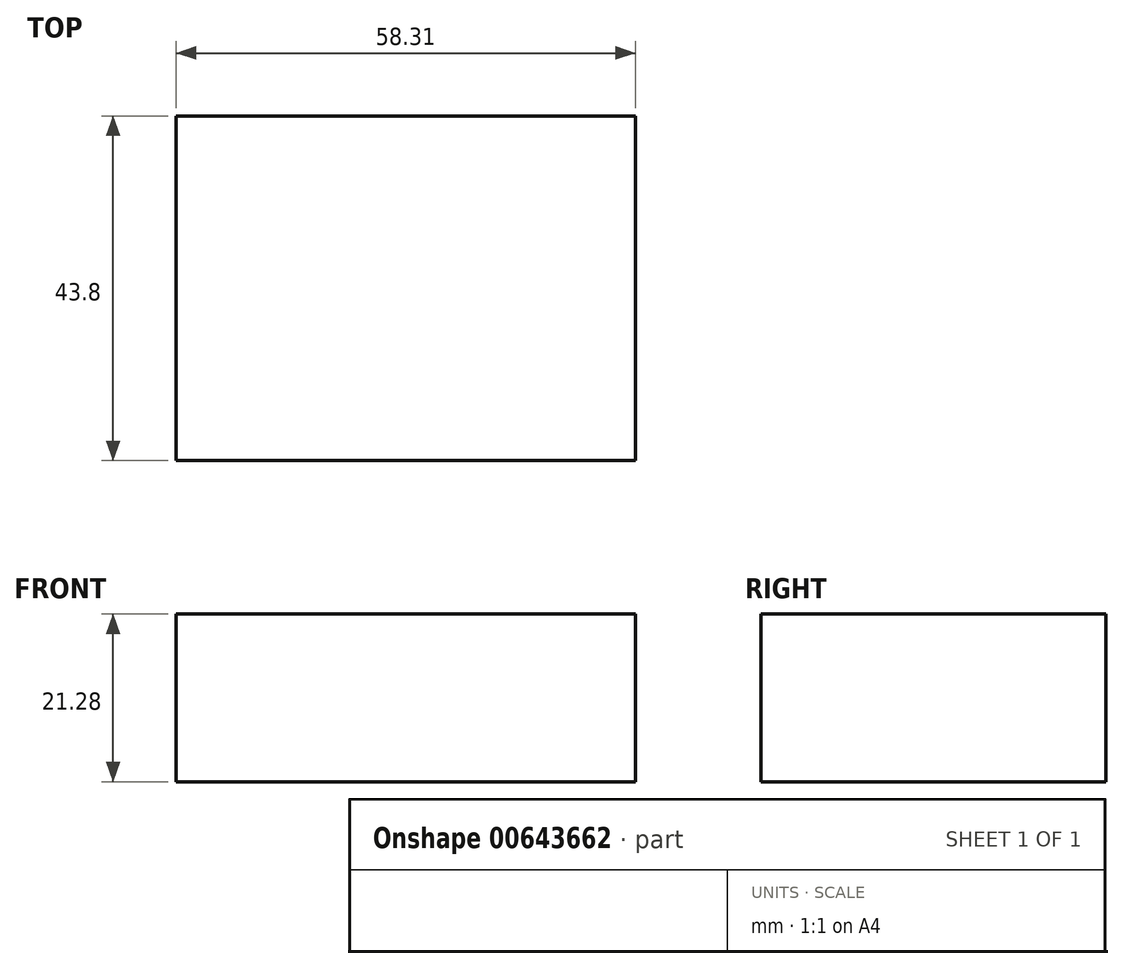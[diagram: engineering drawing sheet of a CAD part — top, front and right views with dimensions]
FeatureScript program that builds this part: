
annotation { "Feature Type Name" : "Feature", "Feature Type Description" : "" }
export const myFeature = defineFeature(function(context is Context, id is Id, definition is map)
    precondition{}
    {
        {
            var Q0;
            Q0=qCreatedBy(makeId("Front.planeOp"),FACE);
            var sketch = newSketch(context, id + "F0", { "sketchPlane" : qUnion([Q0])});
            skLineSegment(sketch, "E0.bottom", {"start": v(-27.47, 0) * mm, "end": v(30.84, 0) * mm});
            skLineSegment(sketch, "E0.top", {"start": v(-27.47, 21.28) * mm, "end": v(30.84, 21.28) * mm});
            skLineSegment(sketch, "E0.left", {"start": v(-27.47, 0) * mm, "end": v(-27.47, 21.28) * mm});
            skLineSegment(sketch, "E0.right", {"start": v(30.84, 0) * mm, "end": v(30.84, 21.28) * mm});
            skSolve(sketch);
        }
        {
            var Q0;
            Q0=makeQuery(id+"F0.imprint","IMPRINT",FACE,{"disambiguationData":[TD([[makeQuery(id+"F0.imprint","IMPRINT",EDGE,{"derivedFrom":sQuery(id+"F0.wireOp",EDGE,"E0.bottom")}),1.0]])]});
            extrude(context, id + "F1", {"entities" : qUnion([Q0]), "depth" : 43.8 * mm, "offsetDistance" : 25 * mm});
        }
    });
